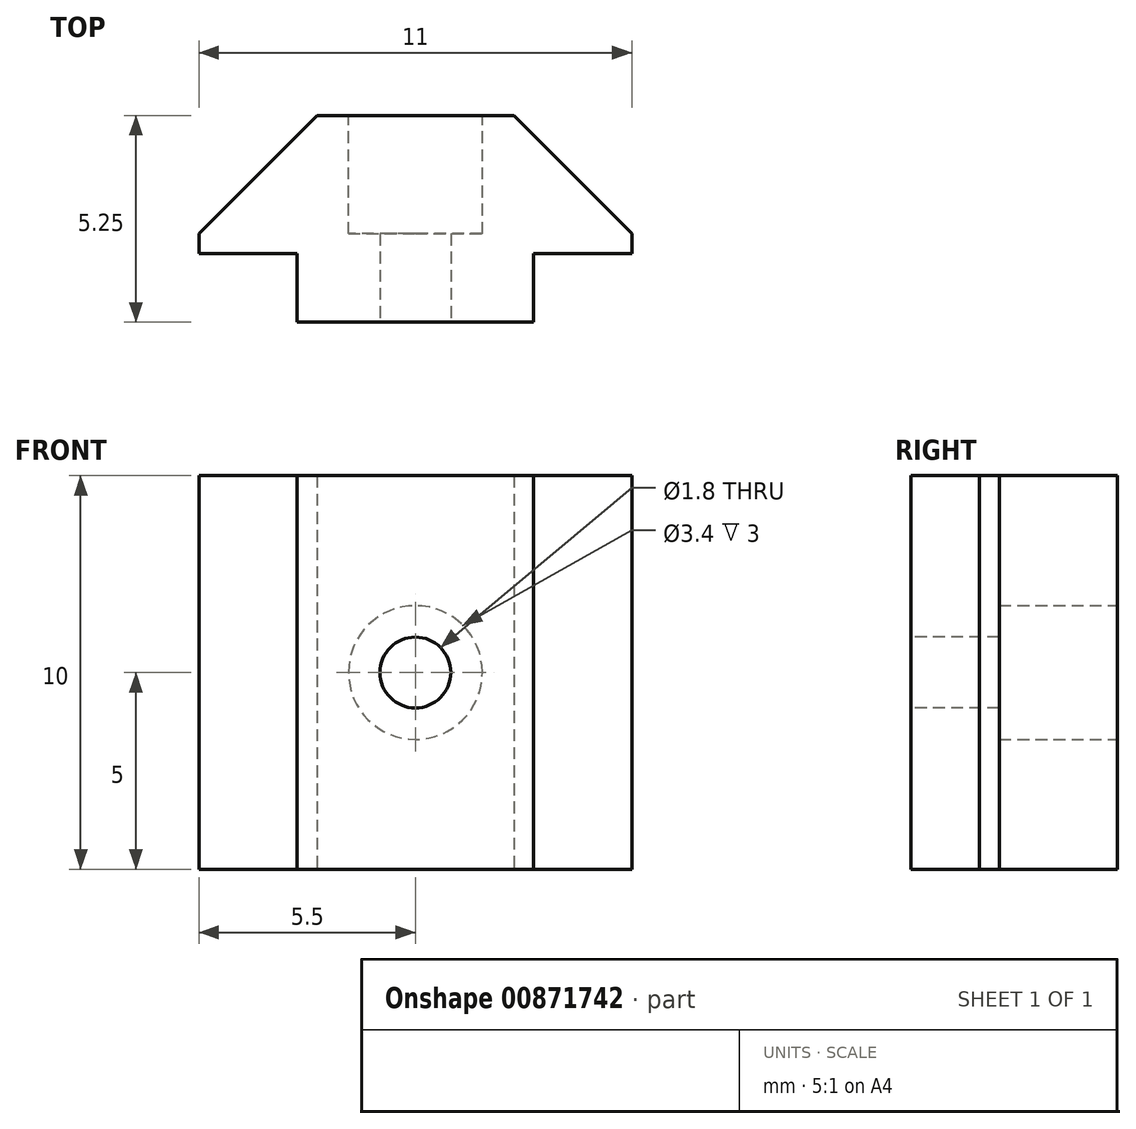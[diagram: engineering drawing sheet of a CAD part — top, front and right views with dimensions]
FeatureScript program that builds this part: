
annotation { "Feature Type Name" : "Feature", "Feature Type Description" : "" }
export const myFeature = defineFeature(function(context is Context, id is Id, definition is map)
    precondition{}
    {
        {
            var Q0;
            Q0=qCreatedBy(makeId("Top.planeOp"),FACE);
            var sketch = newSketch(context, id + "F0", { "sketchPlane" : qUnion([Q0])});
            skLineSegment(sketch, "E0", {"start": v(-3, 0) * mm, "end": v(3, 0) * mm});
            skLineSegment(sketch, "E1", {"start": v(3, 0) * mm, "end": v(3, 1.75) * mm});
            skLineSegment(sketch, "E2", {"start": v(3, 1.75) * mm, "end": v(5.5, 1.75) * mm});
            skLineSegment(sketch, "E3", {"start": v(5.5, 1.75) * mm, "end": v(5.5, 2.25) * mm});
            skLineSegment(sketch, "E4", {"start": v(5.5, 2.25) * mm, "end": v(2.5, 5.25) * mm});
            skLineSegment(sketch, "E5", {"start": v(2.5, 5.25) * mm, "end": v(-2.5, 5.25) * mm});
            skLineSegment(sketch, "E6", {"start": v(-2.5, 5.25) * mm, "end": v(-5.5, 2.25) * mm});
            skLineSegment(sketch, "E7", {"start": v(-5.5, 2.25) * mm, "end": v(-5.5, 1.75) * mm});
            skLineSegment(sketch, "E8", {"start": v(-5.5, 1.75) * mm, "end": v(-3, 1.75) * mm});
            skLineSegment(sketch, "E9", {"start": v(-3, 1.75) * mm, "end": v(-3, 0) * mm});
            skLineSegment(sketch, "E10", {"start": v(-5.5, 2.25) * mm, "end": v(-5.5, 5.25) * mm, "construction": true});
            skLineSegment(sketch, "E11", {"start": v(-2.5, 5.25) * mm, "end": v(-5.5, 5.25) * mm, "construction": true});
            skSolve(sketch);
        }
        {
            var Q0;
            Q0 = qSketchRegion(id + "F0", true);
            extrude(context, id + "F1", {"entities" : qUnion([Q0]), "endBound" : BoundingType.SYMMETRIC, "depth" : 10 * mm, "offsetDistance" : 25 * mm});
        }
        {
            var Q0;
            Q0=makeQuery(id+"F1.opExtrude","SWEPT_FACE",FACE,{"disambiguationData":[OSD([sQuery(id+"F0.wireOp",EDGE,"E0")])]});
            var sketch = newSketch(context, id + "F2", { "sketchPlane" : qUnion([Q0])});
            skCircle(sketch, "E12", {"center": v(0, 0) * mm, "radius": 0.9 * mm});
            skSolve(sketch);
        }
        {
            var Q0;
            Q0 = qSketchRegion(id + "F2", true);
            extrude(context, id + "F3", {"entities" : qUnion([Q0]), "operationType" : NewBodyOperationType.REMOVE, "endBound" : BoundingType.UP_TO_NEXT, "oppositeDirection" : true, "depth" : 25 * mm, "offsetDistance" : 25 * mm});
        }
        {
            var Q0;
            Q0=makeQuery(id+"F1.opExtrude","SWEPT_FACE",FACE,{"disambiguationData":[OSD([sQuery(id+"F0.wireOp",EDGE,"E5")])]});
            var sketch = newSketch(context, id + "F4", { "sketchPlane" : qUnion([Q0])});
            skCircle(sketch, "E13", {"center": v(0, 0) * mm, "radius": 1.7 * mm});
            skSolve(sketch);
        }
        {
            var Q0;
            Q0 = qSketchRegion(id + "F4", true);
            extrude(context, id + "F5", {"entities" : qUnion([Q0]), "operationType" : NewBodyOperationType.REMOVE, "oppositeDirection" : true, "depth" : 3 * mm, "offsetDistance" : 25 * mm});
        }
    });
